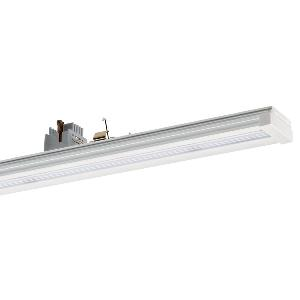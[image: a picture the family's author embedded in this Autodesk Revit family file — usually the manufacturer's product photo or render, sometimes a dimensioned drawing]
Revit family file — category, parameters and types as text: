
# Revit family: conveo_-_cvg_4500_850_w-p_ea_5_226848089-00804944_8a3a
name_source: partatom
category: Lighting Fixtures
units: mm (PartAtom-declared; Revit-internal decimal feet)

## family parameters
Cut with Voids When Loaded = No
Host = Face
Light Source = No
Part Type = Normal
Room Calculation Point = No
Round Connector Dimension = Use Diameter
Shared = No

## types (1)
- CONVEO - CVG 4500/850/W-P/EA/5 (1 x LED, 4600 lm, 5000K)
    Apparent Load = 28 VA
    Approval mark = CE
    CIE Flux Codes = 54 85 97 100 100
    Color Rendering = 80-89
    Color Temperature = 5000K
    Control Gear = Electronic ballast
    Default Elevation = 1800 mm
    Description = CVG 4500/850/W-P/EA/5|Continuous-row system|light source: LED|work equipment: Electronic ballast|connected load: 220-240 V, 50-60 Hz|Power consumption: approx. 28 W|luminous flux: 4600 lm|luminous efficacy: 164 lm/W|colour temperature: Cold white, ca. 5000 K|color rendering index (CRI): >= 80|chromaticity tolerance:  3 SDCM|System of protection: IP 54|class of protection: I|technology: Switchable|luminaire body|material: Aluminium|surface: Powder coatet|colour: White|lamp cover: Acrylic (PMMA), Satine|weight (net): approx. 1.9 kg|Fastening: Available separately|minimum ambient temperature: -25 ░C|maximum ambient temperature: 56 ░C|glare control: Prism optics (linear)|Approval mark: VDE - ENEC|
    Frequency = 50 Hz
    Height = 70 mm
    Lamp = 1 x LED
    Lamp Light Flux = 4600 lm
    Lamp count = 1
    Length = 1500 mm
    Luminous efficacy = 164 lm/W
    Manufacturer = Waldmann
    ModVariant = No
    Model = 226848089-00804944
    Mounting Place = Ceiling
    Mounting Type = Pendant
    Number of Poles = 1
    OnlyDefault = Yes
    Power Factor = 1
    Product Name = CONVEO - CVG 4500/850/W-P/EA/5
    Product group = Continuous-row system (industry)
    ProductGroupID = 301
    Protection Class = Protection class I
    Protection Degree = IP 54
    RLX_Detail_Level = 1
    RlxData = <blob elided: 99109 chars, md5=0dd70611>
    Socket = socket
    Standby Power = 0 W
    System Light Flux = 4600 lm
    System Power = 28 W
    Type Comments = Product without accessories
    Type Image = 226848079-00804943-1p5.jpg
    URL = http://relux.com
    VarID = ---
    Voltage = 230 V
    Voltage Range = 220-240 V
    Weight = 0.00 kg
    Width = 64 mm

## geometry (parser evidence)
native form markers: Blend x4, Sweep x9
no freeform markers — native parametric forms only
